# Revit family: Lighting_Pendants_Zero_Bob_Bow
name_source: partatom
category: Lighting Fixtures
revit_build: Autodesk Revit 2018 (Build: 20170223_1515(x64)
units: mm (PartAtom-declared; Revit-internal decimal feet)

## family parameters
Always vertical = Yes
Cut with Voids When Loaded = No
Light Source = No
Part Type = Normal
Room Calculation Point = No
Round Connector Dimension = Use Diameter
Shared = No
Work Plane-Based = Yes

## types (2) — shared parameters
Apparent Load = 0 VA
AssetType = Fixed
BIMObjectName = Lighting_Pendants_Zero_Bob_Bow
Brand = Zero
Category = Pendants
Collection = Bob
ColourRenderingIndex = >80
ConvergoRefNr = 0046-2005-0001-SE
Description = In collaboration with well-known furniture brand Blå Station, their BOB sofa system has been given a fixture that takes its contours to new heights while being anchored in the backrest. Zero also offers afreestanding floor-lamp version and a pendant with the same likeable, round character. A dimmable LED behind a convex glare shield provides intimate and screened-off illumination; available in standard black or white.New for 2020, this fixture is now available as a bow that billows over the BOB sofa. The distance between the lights follows the same mathematics asthe sofa modules. This new version works well over sofas, in corridors, above conference tables, etc.
Designer = Thomas Bernstrand & Stefan Borselius 2020.
Dimmer = Dimmable 230V
DurationUnit = Hours
ElectricalDeviceNominalPower = 30 W
ExpectedLife = L70 >50.000h
Features = Suspended from ceiling 2,5 m cable. DCL ceiling-plug or terminal-block 3x4 mm2.
Finish = Painted aluminum and steel. White RAL 9010, black RAL 9005. Diffusor in matt acrylic. Other colours on request.
HasProtectiveEarth = No
IP_Code = IP20
IfcExportAs = IfcLightFixtureType
IfcExportType = NOTDEFINED
LightFixtureMountingType = Suspended
LightFixturePlacingType = Ceilling
LightFixtureSecondaryMaterial = Mat Acrylic
Manufacturer = Zero
ManufacturerName = Zero
ManufacturerURL = https://www.zerolighting.com
Material = Aluminium/steel.
NBSDescription = General purpose luminaires
NBSReference = 90-60-50/405
Name = Zero_Bob_Bow
NominalCurrent = 0 A
NominalDepth = 261 mm
NominalFrequencyRange = 50 Hz
NominalHeight = 633 mm
NominalLength = 2340 mm  [stored 7.67717 ft]
NominalVoltage = 230 V
NominalVoltageCalc = 0 V
NumberOfPoles = 1
NumberOfSources = 1
PhaseAngle = 0.00°
ProductDatasheet = https://www.zerolighting.com
Shape = Sculptured
Size = 2340x260x635 mm
TotalWattage = 30 W
URL = https://www.zerolighting.com
Uniclass2 = Pr_70_70_49_86
Uniclass2015Description = Suspended luminaires
Uniclass2015Reference = Pr_70_70_48_86
UsageCurrent = 0 A
Version = 1
VersionDate = 11/05/2020
WarrantyDurationUnit = Year
zero-valued in all types: DefaultElevation, MaintenanceFactor

## per-type parameters (varying)
| type | ArticleNumber | Color | LightFixtureMainMaterial | LightSource | ModelReference |
| Bob Bow Pendant - Black | 19102306-30 | Black | Black 9005 RAL | System power: 30W. Luminaire Luminous Flux: 2514LM. CCT 3000K. SDCM 3. CRI 80. Dimmable 230V. 
L70 >50.000h. | 19102306-30 |
| Bob Bow Pendant - White | 19102301-30 | White | White RAL 9010 | System power: 30W. Luminaire Luminous Flux: 2514LM. CCT 3000K. SDCM 3. CRI 80. Dimmable 230V. | 19102301-30 |

note: column(s) folded — value = type name in every type: Model

note: [stored X ft] marks values corroborated as IEEE doubles in the binary element streams (Revit-internal decimal feet)

## geometry (parser evidence)
native form markers: Sweep x7
no freeform markers — native parametric forms only
